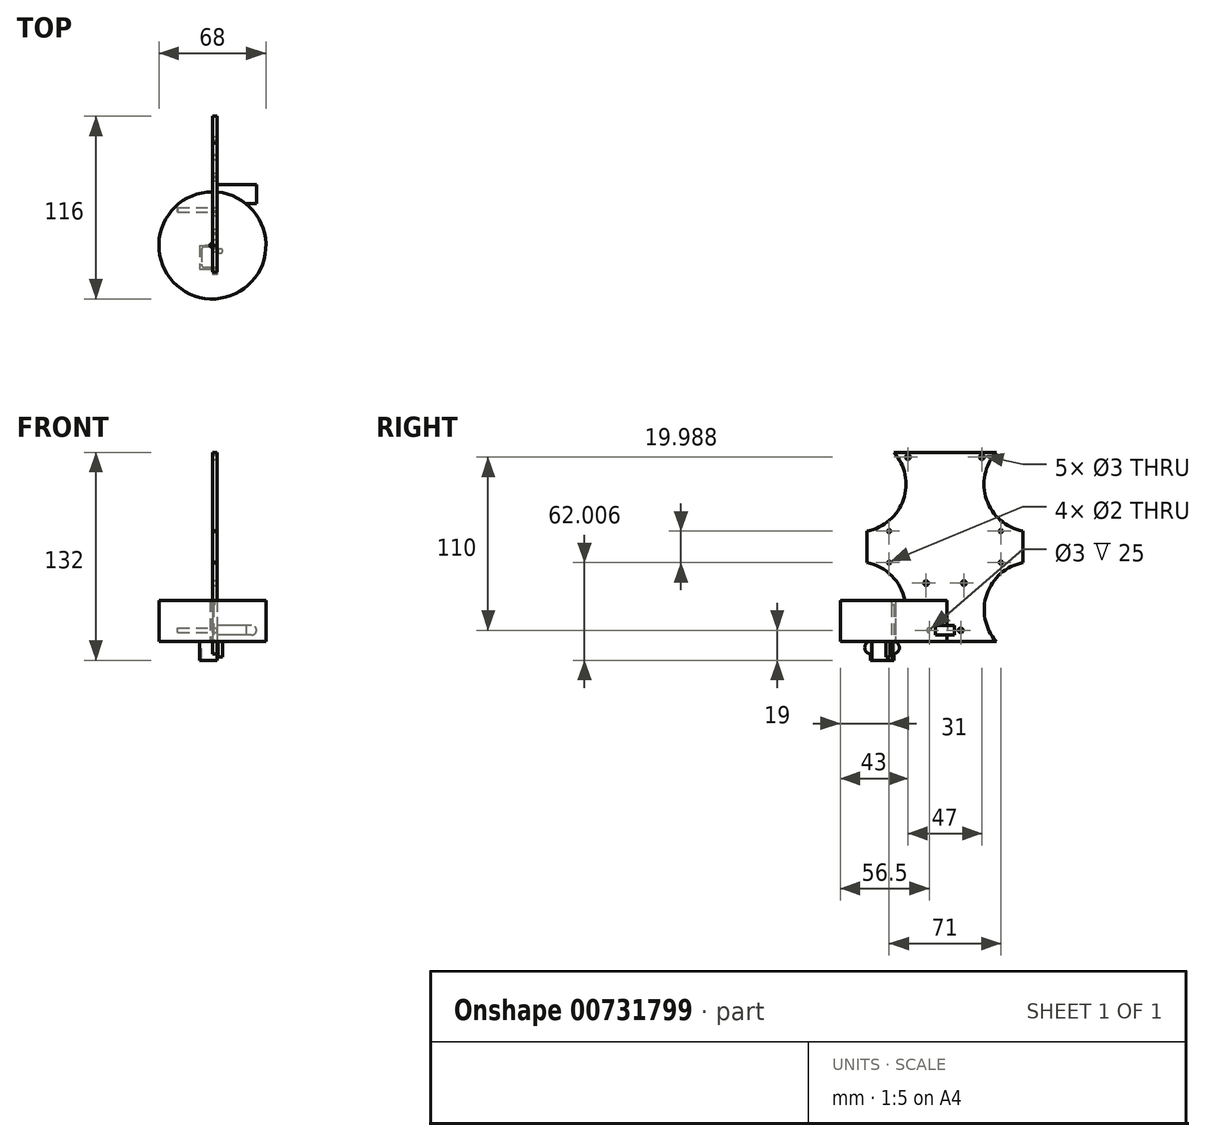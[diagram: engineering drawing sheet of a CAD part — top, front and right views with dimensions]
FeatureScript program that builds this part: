
annotation { "Feature Type Name" : "Feature", "Feature Type Description" : "" }
export const myFeature = defineFeature(function(context is Context, id is Id, definition is map)
    precondition{}
    {
        {
            var Q0;
            Q0=qCreatedBy(makeId("Top.planeOp"),FACE);
            var sketch = newSketch(context, id + "F0", { "sketchPlane" : qUnion([Q0])});
            skCircle(sketch, "E0", {"center": v(0, 0) * mm, "radius": 34 * mm});
            skSolve(sketch);
        }
        {
            var Q0;
            Q0 = qSketchRegion(id + "F0", true);
            extrude(context, id + "F1", {"entities" : qUnion([Q0]), "depth" : 26 * mm, "offsetDistance" : 25 * mm});
        }
        {
            var Q0;
            Q0=makeQuery(id+"F1.opExtrude","CAP_FACE",FACE,{"disambiguationData":[OSD([sQuery(id+"F0.wireOp",EDGE,"E0")])],"isStart":true});
            var sketch = newSketch(context, id + "F2", { "sketchPlane" : qUnion([Q0])});
            skArc(sketch, "E1", {"start": v(1.12, -1) * mm, "mid": v(0, 1.5) * mm, "end": v(-1.12, -1) * mm});
            skLineSegment(sketch, "E2", {"start": v(1.12, -1) * mm, "end": v(-1.12, -1) * mm});
            skSolve(sketch);
        }
        {
            var Q0;
            Q0 = qSketchRegion(id + "F2", true);
            extrude(context, id + "F3", {"entities" : qUnion([Q0]), "operationType" : NewBodyOperationType.REMOVE, "oppositeDirection" : true, "depth" : 26 * mm, "offsetDistance" : 25 * mm});
        }
        {
            var Q0;
            Q0=qCreatedBy(makeId("Top.planeOp"),FACE);
            var sketch = newSketch(context, id + "F4", { "sketchPlane" : qUnion([Q0])});
            skLineSegment(sketch, "E3", {"start": v(0, 0) * mm, "end": v(0, -7) * mm});
            skLineSegment(sketch, "E4", {"start": v(10, -7) * mm, "end": v(10, 0) * mm});
            skArc(sketch, "E5", {"start": v(0, -7) * mm, "mid": v(5, -9.75) * mm, "end": v(10, -7) * mm});
            skArc(sketch, "E6", {"start": v(10, 0) * mm, "mid": v(5, 2.75) * mm, "end": v(0, 0) * mm});
            skPoint(sketch, "E7.orphan", {"position": v(5, -7) * mm});
            skPoint(sketch, "E8.start.orphan", {"position": v(5, 0) * mm});
            skSolve(sketch);
        }
        {
            var Q0;
            Q0 = qSketchRegion(id + "F4", true);
            extrude(context, id + "F5", {"entities" : qUnion([Q0]), "depth" : 23 * mm, "offsetDistance" : 25 * mm});
        }
        {
            var Q0;
            Q0=makeQuery(id+"F5.opExtrude","CAP_FACE",FACE,{"disambiguationData":[OSD([sQuery(id+"F4.wireOp",EDGE,"E3"),sQuery(id+"F4.wireOp",EDGE,"E4"),sQuery(id+"F4.wireOp",EDGE,"E5"),sQuery(id+"F4.wireOp",EDGE,"E6")])],"isStart":true});
            var sketch = newSketch(context, id + "F6", { "sketchPlane" : qUnion([Q0])});
            skArc(sketch, "E9", {"start": v(6.12, 2.5) * mm, "mid": v(5, 5) * mm, "end": v(3.88, 2.5) * mm});
            skLineSegment(sketch, "E10", {"start": v(6.12, 2.5) * mm, "end": v(3.88, 2.5) * mm});
            skSolve(sketch);
        }
        {
            var Q0;
            Q0 = qSketchRegion(id + "F6", true);
            extrude(context, id + "F7", {"entities" : qUnion([Q0]), "operationType" : NewBodyOperationType.ADD, "depth" : 10 * mm, "offsetDistance" : 25 * mm});
        }
        {
            var Q0;
            Q0=qCreatedBy(makeId("Right.planeOp"),FACE);
            var sketch = newSketch(context, id + "F8", { "sketchPlane" : qUnion([Q0])});
            skLineSegment(sketch, "E11", {"start": v(0, 0) * mm, "end": v(-15, 0) * mm});
            skLineSegment(sketch, "E12", {"start": v(-15, -12) * mm, "end": v(0, -12) * mm});
            skLineSegment(sketch, "E13", {"start": v(0, -12) * mm, "end": v(0, -8) * mm});
            skArc(sketch, "E14", {"start": v(0, -8) * mm, "mid": v(3.5, -4) * mm, "end": v(0, 0) * mm});
            skPoint(sketch, "E15.orphan", {"position": v(0, -4) * mm});
            skPoint(sketch, "E16.MirrorP", {"position": v(-15, -4) * mm});
            skArc(sketch, "E17.MirrorCS", {"start": v(-15, -8) * mm, "mid": v(-18.5, -4) * mm, "end": v(-15, 0) * mm});
            skLineSegment(sketch, "E18.trimOffspring", {"start": v(-15, -8) * mm, "end": v(-15, -12) * mm});
            skSolve(sketch);
        }
        {
            var Q0;
            Q0=makeQuery(id+"F8.imprint","IMPRINT",FACE,{"disambiguationData":[TD([[makeQuery(id+"F8.imprint","IMPRINT",EDGE,{"derivedFrom":sQuery(id+"F8.wireOp",EDGE,"E11")}),1.0]])]});
            extrude(context, id + "F9", {"entities" : qUnion([Q0]), "depth" : 3 * mm, "offsetDistance" : 25 * mm});
        }
        {
            var Q0;
            Q0=makeQuery(id+"F9.opExtrude","CAP_FACE",FACE,{"disambiguationData":[OSD([sQuery(id+"F8.wireOp",EDGE,"E11"),sQuery(id+"F8.wireOp",EDGE,"E12"),sQuery(id+"F8.wireOp",EDGE,"E13"),sQuery(id+"F8.wireOp",EDGE,"E14"),sQuery(id+"F8.wireOp",EDGE,"E17.MirrorCS"),sQuery(id+"F8.wireOp",EDGE,"E18.trimOffspring")])],"isStart":true});
            var sketch = newSketch(context, id + "F10", { "sketchPlane" : qUnion([Q0])});
            skLineSegment(sketch, "E19.bottom", {"start": v(0, 0) * mm, "end": v(15, 0) * mm});
            skLineSegment(sketch, "E19.top", {"start": v(0, -12) * mm, "end": v(15, -12) * mm});
            skLineSegment(sketch, "E19.left", {"start": v(0, 0) * mm, "end": v(0, -12) * mm});
            skLineSegment(sketch, "E19.right", {"start": v(15, 0) * mm, "end": v(15, -12) * mm});
            skSolve(sketch);
        }
        {
            var Q0;
            Q0 = qSketchRegion(id + "F10", true);
            extrude(context, id + "F11", {"entities" : qUnion([Q0]), "operationType" : NewBodyOperationType.ADD, "depth" : 8 * mm, "offsetDistance" : 25 * mm});
        }
        {
            var Q0;
            Q0=makeQuery(id+"F11.boolean.opBoolean","MERGE",FACE,{"derivedFrom":[makeQuery(id+"F9.opExtrude","SWEPT_FACE",FACE,{"disambiguationData":[OSD([sQuery(id+"F8.wireOp",EDGE,"E11")])]}),makeQuery(id+"F11.opExtrude","SWEPT_FACE",FACE,{"disambiguationData":[OSD([sQuery(id+"F10.wireOp",EDGE,"E19.bottom")])]})]});
            var sketch = newSketch(context, id + "F12", { "sketchPlane" : qUnion([Q0])});
            skLineSegment(sketch, "E20", {"start": v(3, -1) * mm, "end": v(-5, -1) * mm});
            skLineSegment(sketch, "E21", {"start": v(3, -14) * mm, "end": v(3, -1) * mm});
            skPoint(sketch, "E22.visualSharp", {"position": v(-7, -14) * mm});
            skPoint(sketch, "E23.visualSharp", {"position": v(-7, -12) * mm});
            skLineSegment(sketch, "E24", {"start": v(-7, -3) * mm, "end": v(-7, -12) * mm});
            skLineSegment(sketch, "E25", {"start": v(3, -14) * mm, "end": v(-5, -14) * mm});
            skArc(sketch, "E26.filletArc", {"start": v(-7, -12) * mm, "mid": v(-6.41, -13.41) * mm, "end": v(-5, -14) * mm});
            skPoint(sketch, "E27.visualSharp", {"position": v(-7, -1) * mm});
            skArc(sketch, "E27.filletArc", {"start": v(-5, -1) * mm, "mid": v(-6.41, -1.59) * mm, "end": v(-7, -3) * mm});
            skSolve(sketch);
        }
        {
            var Q0;
            Q0 = qSketchRegion(id + "F12", true);
            extrude(context, id + "F13", {"entities" : qUnion([Q0]), "operationType" : NewBodyOperationType.REMOVE, "oppositeDirection" : true, "depth" : 25 * mm, "offsetDistance" : 25 * mm});
        }
        {
            var Q0;
            Q0=qCreatedBy(makeId("Right.planeOp"),FACE);
            var sketch = newSketch(context, id + "F14", { "sketchPlane" : qUnion([Q0])});
            skLineSegment(sketch, "E28", {"start": v(-17, 50) * mm, "end": v(-17, 70) * mm});
            skLineSegment(sketch, "E29", {"start": v(82, 70) * mm, "end": v(82, 50) * mm});
            skPoint(sketch, "E30.trimOffspring.start.orphan", {"position": v(65, 120) * mm});
            skPoint(sketch, "E31.start.orphan", {"position": v(0, 0) * mm});
            skLineSegment(sketch, "E32", {"start": v(-17, 70) * mm, "end": v(-17, 50) * mm});
            skPoint(sketch, "E33.MirrorP", {"position": v(65, 0) * mm});
            skLineSegment(sketch, "E34.MirrorCS", {"start": v(82, 50) * mm, "end": v(82, 70) * mm});
            skPoint(sketch, "E35.orphan", {"position": v(82, 120) * mm});
            skPoint(sketch, "E36.orphan", {"position": v(82, 0) * mm});
            skPoint(sketch, "E37.orphan", {"position": v(-17, 0) * mm});
            skPoint(sketch, "E38.orphan", {"position": v(-17, 120) * mm});
            skPoint(sketch, "E39.end.orphan", {"position": v(32.5, 0) * mm});
            skPoint(sketch, "E40.end.orphan", {"position": v(32.5, 120) * mm});
            skPoint(sketch, "E41.start.orphan", {"position": v(0, 120) * mm});
            skPoint(sketch, "E42.start.orphan", {"position": v(0, 50) * mm});
            skLineSegment(sketch, "E43", {"start": v(0, 0) * mm, "end": v(65, 0) * mm});
            skLineSegment(sketch, "E44", {"start": v(0, 120) * mm, "end": v(65, 120) * mm});
            skArc(sketch, "E45", {"start": v(65, 120) * mm, "mid": v(58.92, 90.04) * mm, "end": v(82, 70) * mm});
            skArc(sketch, "E46", {"start": v(82, 50) * mm, "mid": v(59.04, 29.92) * mm, "end": v(65, 0) * mm});
            skArc(sketch, "E47.MirrorCS", {"start": v(-17, 50) * mm, "mid": v(5.96, 29.92) * mm, "end": v(0, 0) * mm});
            skArc(sketch, "E48.MirrorCS", {"start": v(0, 120) * mm, "mid": v(6.08, 90.04) * mm, "end": v(-17, 70) * mm});
            skSolve(sketch);
        }
        {
            var Q0;
            Q0 = qSketchRegion(id + "F14", true);
            extrude(context, id + "F15", {"entities" : qUnion([Q0]), "depth" : 3 * mm, "offsetDistance" : 25 * mm});
        }
        {
            var Q0;
            Q0=makeQuery(id+"F15.opExtrude","CAP_FACE",FACE,{"disambiguationData":[OSD([sQuery(id+"F14.wireOp",EDGE,"E34.MirrorCS"),sQuery(id+"F14.wireOp",EDGE,"E43"),sQuery(id+"F14.wireOp",EDGE,"E44"),sQuery(id+"F14.wireOp",EDGE,"E45"),sQuery(id+"F14.wireOp",EDGE,"E46"),sQuery(id+"F14.wireOp",EDGE,"E47.MirrorCS"),sQuery(id+"F14.wireOp",EDGE,"E48.MirrorCS"),sQuery(id+"F14.wireOp",EDGE,"E28")])],"isStart":false});
            var sketch = newSketch(context, id + "F16", { "sketchPlane" : qUnion([Q0])});
            skLineSegment(sketch, "E49", {"start": v(26.5, 4) * mm, "end": v(38.5, 4) * mm});
            skLineSegment(sketch, "E50", {"start": v(26.5, 4) * mm, "end": v(26.5, 10) * mm});
            skLineSegment(sketch, "E51", {"start": v(26.5, 10) * mm, "end": v(38.5, 10) * mm});
            skLineSegment(sketch, "E52", {"start": v(38.5, 10) * mm, "end": v(38.5, 4) * mm});
            skSolve(sketch);
        }
        {
            var Q0;
            Q0 = qSketchRegion(id + "F16", true);
            extrude(context, id + "F17", {"entities" : qUnion([Q0]), "operationType" : NewBodyOperationType.ADD, "depth" : 25 * mm, "offsetDistance" : 25 * mm});
        }
        {
            var Q0;
            Q0=makeQuery(id+"F15.opExtrude","CAP_FACE",FACE,{"disambiguationData":[OSD([sQuery(id+"F14.wireOp",EDGE,"E34.MirrorCS"),sQuery(id+"F14.wireOp",EDGE,"E43"),sQuery(id+"F14.wireOp",EDGE,"E44"),sQuery(id+"F14.wireOp",EDGE,"E45"),sQuery(id+"F14.wireOp",EDGE,"E46"),sQuery(id+"F14.wireOp",EDGE,"E47.MirrorCS"),sQuery(id+"F14.wireOp",EDGE,"E48.MirrorCS"),sQuery(id+"F14.wireOp",EDGE,"E28")])],"isStart":false});
            var sketch = newSketch(context, id + "F18", { "sketchPlane" : qUnion([Q0])});
            skCircle(sketch, "E53", {"center": v(68, 50) * mm, "radius": 1 * mm});
            skCircle(sketch, "E54.MirrorC", {"center": v(68, 70) * mm, "radius": 1 * mm});
            skCircle(sketch, "E55.MirrorC", {"center": v(-3, 50) * mm, "radius": 1 * mm});
            skCircle(sketch, "E56.MirrorC", {"center": v(-3, 70) * mm, "radius": 1 * mm});
            skCircle(sketch, "E57", {"center": v(22.5, 7) * mm, "radius": 1.5 * mm});
            skPoint(sketch, "E58.orphan", {"position": v(26.5, 7) * mm});
            skPoint(sketch, "E59.MirrorP", {"position": v(38.5, 7) * mm});
            skCircle(sketch, "E60.MirrorC", {"center": v(42.5, 7) * mm, "radius": 1.5 * mm});
            skCircle(sketch, "E61", {"center": v(9, 117) * mm, "radius": 1.5 * mm});
            skCircle(sketch, "E62", {"center": v(56, 117) * mm, "radius": 1.5 * mm});
            skCircle(sketch, "E63", {"center": v(20.5, 37) * mm, "radius": 1.5 * mm});
            skCircle(sketch, "E64.MirrorC", {"center": v(44.5, 37) * mm, "radius": 1.5 * mm});
            skPoint(sketch, "E65.orphan", {"position": v(22.5, 37) * mm});
            skPoint(sketch, "E66.orphan", {"position": v(42.5, 37) * mm});
            skPoint(sketch, "E67.start.orphan", {"position": v(32.5, 10) * mm});
            skSolve(sketch);
        }
        {
            var Q0;
            Q0=makeQuery(id+"F17.opExtrude","CAP_EDGE",EDGE,{"disambiguationData":[OSD([sQuery(id+"F16.wireOp",EDGE,"E51")])],"isStart":false});
            var Q1;
            Q1=makeQuery(id+"F17.opExtrude","CAP_EDGE",EDGE,{"disambiguationData":[OSD([sQuery(id+"F16.wireOp",EDGE,"E49")])],"isStart":false});
            fillet(context, id + "F19", {"entities" : qUnion([Q0, Q1]), "radius" : 3 * mm, "tangentPropagation" : true, "allowEdgeOverflow" : false});
        }
        {
            var Q0;
            Q0 = qSketchRegion(id + "F18", true);
            extrude(context, id + "F20", {"entities" : qUnion([Q0]), "operationType" : NewBodyOperationType.REMOVE, "oppositeDirection" : true, "depth" : 25 * mm, "offsetDistance" : 25 * mm});
        }
    });
